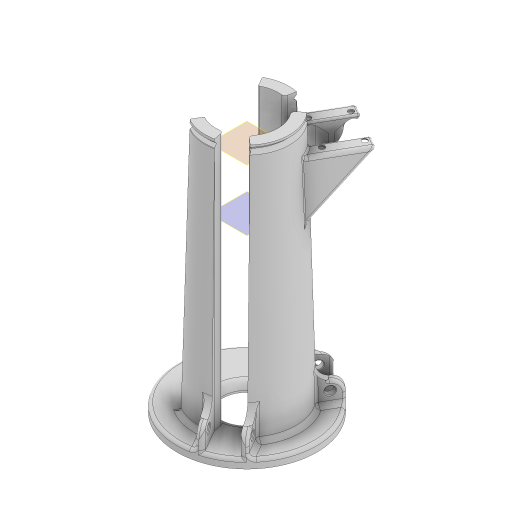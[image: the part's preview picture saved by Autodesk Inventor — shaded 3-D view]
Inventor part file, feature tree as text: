
AUTODESK INVENTOR PART (.ipt)
format: ipt  version: 2023 (Build 270158000, 158)  size: 1,966,080 bytes
history: native  units: in
note: dims shown in document units (in); Inventor stores cm internally (conversion verified against a paired STEP export)
features: fillet x16, projected_geometry x8, sketch x6, plane x6, extrude x4, hole x2, draft x2, pattern_circular x1, revolve x1, chamfer x1, mirror x1
ambient origin geometry x8: Origin, YZ Plane, XZ Plane, XY Plane, X Axis, Y Axis, Z Axis, Center Point
bodies: Solid1 (feature_tree)
feature tree (48):
  sketch  "Sketch2"  dims[d0=1.0in d1=1.4038in]
  extrude  "Extrusion1"  Depth=1.4038in
  extrude  "Extrusion2"  TaperAngle=120.0deg  [1 undecoded]
  extrude  "Extrusion3"  Depth=0.481in
  hole  "Hole1"  [1 undecoded]
  pattern_circular  "Circular Pattern1"  [2 undecoded]
  sketch  "Sketch5"  dims[d4=0.5906in d5=0.481in]
  fillet  "Fillet1"  Radius=5.9055in
  plane  "Work Plane3"
  plane  "Work Plane2"
  revolve  "Revolution1"  [1 undecoded]
  draft  "FaceDraft6"
  plane  "Work Plane6"
  plane  "Work Plane7"
  plane  "Work Plane5"
  sketch  "Sketch16"  dims[d13=120.0deg d14=0.1969in d15=0.0in d17=5.9055in d18=0.0in d19=0.1378in d20=0.1378in d21=0.5906in d22=0.4961in d23=0.0in d24=0.7874in d25=120.0deg d28=0.1831in d29=0.2362in d30=0.1575in d31=0.0787in d32=90.0deg d33=0.315in d34=0.8108in d35=0.3937in d39=1.0945in d40=0.0787in d66=0.1181in d67=0.0787in d68=360.0deg d69=-0.6427in d70=1.1024in d72=0.3228in d73=0.7087in d74=0.1736in d76=0.122in d77=0.122in d82=0.2953in d83=0.2559in d84=0.2362in d85=0.1575in d86=0.0787in d87=90.0deg d88=1.2992in d89=90.0deg d104=0.1831in d107=0.0103in d123=0.2756in d124=0.0984in d125=0.1575in d126=0.0787in d127=0.0157in d128=0.0787in d129=45.0deg d146=0.6118in d147=90.0deg d148=90.0deg d150=1.378in d151=0.0in d152=-0.2886in d153=0.1171in d154=0.1171in d155=0.0394in d156=0.3937in d157=0.1969in d158=0.3937in d159=0.0394in d160=0.0787in d161=0.0689in d162=0.0787in d164=0.0984in d165=0.0197in d166=0.0197in d106=0.0197in d108=0.0197in d109=0.0344in d113=0.0197in d114=0.0344in d115=0.0197in d116=0.0344in]
  fillet  "Fillet15"  Radius=0.1378in
  fillet  "Fillet16"  Radius=0.5906in
  fillet  "Fillet17"  Radius=0.4961in
  fillet  "Fillet18"  Radius=0.7874in
  chamfer  "Chamfer1"  Distance=0.3937in
  sketch  "Sketch11"  dims[d11=0.8987in]
  extrude  "Extrusion14"  Depth=1.0945in
  hole  "Hole3"  [1 undecoded]
  plane  "Work Plane4"
  draft  "FaceDraft8"
  mirror  "Mirror4"
  fillet  "Fillet21"  Radius=0.1181in
  fillet  "Fillet22"  Radius=0.0787in
  fillet  "Fillet23"  [1 undecoded]
  fillet  "Fillet24"  [1 undecoded]
  fillet  "Fillet25"  Radius=1.1024in
  fillet  "Fillet26"  Radius=0.3228in
  fillet  "Fillet27"  Radius=0.7087in
  fillet  "Fillet28"  Radius=0.1736in
  fillet  "Fillet30"  Radius=0.122in
  fillet  "Fillet31"  Radius=0.122in
  fillet  "Fillet32"  Radius=0.2953in
  sketch  "Sketch3"  dims[d2=3.1496in d3=120.0deg]
  projected_geometry  "Projected Loop1"
  projected_geometry  "Projected Loop2"
  projected_geometry  "Projected Loop3"
  projected_geometry  "Projected Loop4"
  projected_geometry  "Projected Loop5"
  sketch  "Sketch10"  dims[d6=0.8987in d7=0.7874in d9=120.0deg]
  projected_geometry  "Projected Loop8"
  projected_geometry  "Project Cut Edges1"
  projected_geometry  "Project Cut Edges2"
note: 8 required parameter values undecoded (feature->parameter linkage not recoverable at this tier; creation-order binding heuristic only, values carry confidence <= 0.55)